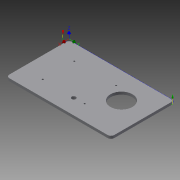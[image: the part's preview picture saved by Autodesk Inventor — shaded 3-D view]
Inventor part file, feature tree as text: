
AUTODESK INVENTOR PART (.ipt)
format: ipt  version: 2015 SP1 (Build 190203100, 203)  size: 393,216 bytes
history: native  units: mm
features: extrude x2, sketch x2, hole x1, pattern_linear x1, fillet x1
ambient origin geometry x8: Origin, YZ Plane, XZ Plane, XY Plane, X Axis, Y Axis, Z Axis, Center Point
bodies: Solid1 (feature_tree)
feature tree (7):
  extrude  "Extrusion1"  Depth=5.0mm
  extrude  "Extrusion2"  Depth=6.0mm
  hole  "Hole1"  [1 undecoded]
  pattern_linear  "Rectangular Pattern1"  Count1=7  [1 undecoded]
  fillet  "Fillet1"  Radius=150.0mm
  sketch  "Sketch1"  dims[d2=5.0mm d3=0.0mm d4=74.0mm]
  sketch  "Sketch2"  dims[d5=30.0mm d6=30.0mm d7=85.0mm d8=70.0mm d9=150.0mm d10=8.0mm d11=42.0mm d13=8.0mm d14=0.0mm d15=40.0mm d16=30.0mm d17=3.0mm d18=6.0mm d19=4.0mm d20=2.0mm d21=90.0deg d22=8.0mm d23=20.594885mm d24=20.0mm d26=80.0mm d27=20.0mm d29=60.0mm d30=6.0mm]
note: 2 required parameter values undecoded (feature->parameter linkage not recoverable at this tier; creation-order binding heuristic only, values carry confidence <= 0.55)
